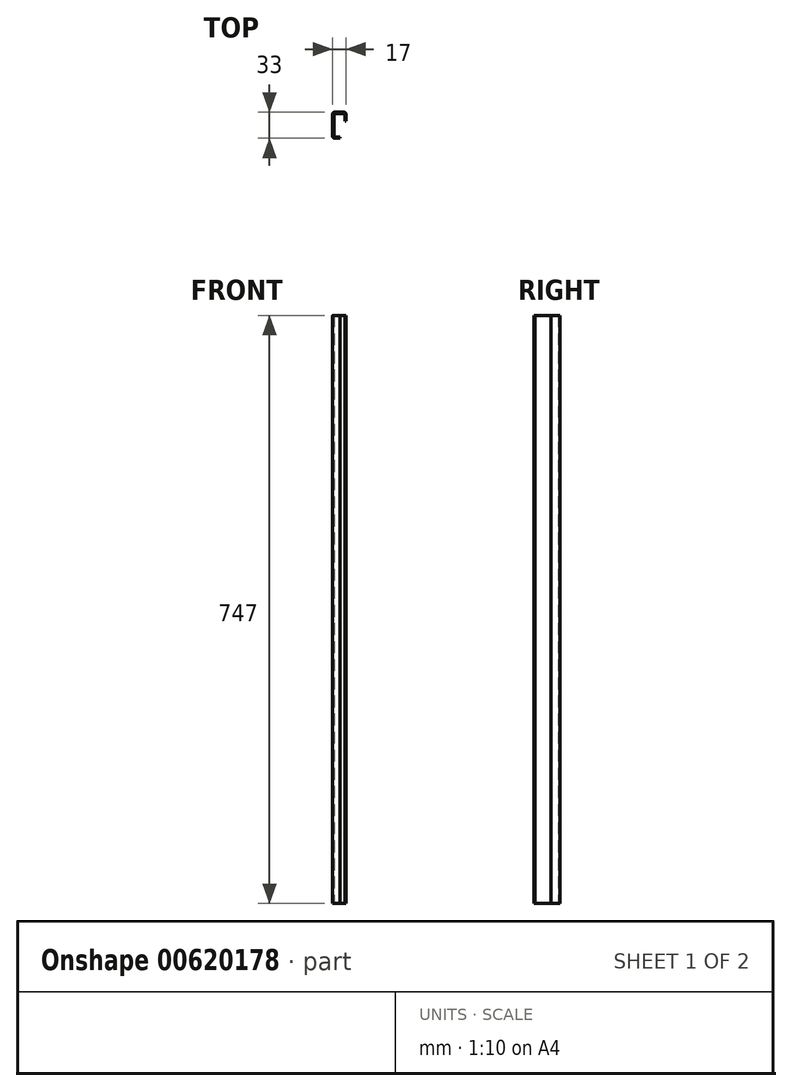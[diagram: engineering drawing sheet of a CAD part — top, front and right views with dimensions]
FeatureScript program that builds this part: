
annotation { "Feature Type Name" : "Feature", "Feature Type Description" : "" }
export const myFeature = defineFeature(function(context is Context, id is Id, definition is map)
    precondition{}
    {
        {
            var Q0;
            Q0=qCreatedBy(makeId("Top.planeOp"),FACE);
            var sketch = newSketch(context, id + "F0", { "sketchPlane" : qUnion([Q0])});
            skLineSegment(sketch, "E0", {"start": v(9.5, -16.5) * mm, "end": v(2.5, -16.5) * mm});
            skLineSegment(sketch, "E1", {"start": v(0, -14) * mm, "end": v(0, 14) * mm});
            skLineSegment(sketch, "E2", {"start": v(2.5, 16.5) * mm, "end": v(14.5, 16.5) * mm});
            skLineSegment(sketch, "E3", {"start": v(17, 14) * mm, "end": v(17, 5.5) * mm});
            skPoint(sketch, "E4.visualSharp", {"position": v(0, 16.5) * mm});
            skArc(sketch, "E4.filletArc", {"start": v(2.5, 16.5) * mm, "mid": v(0.73, 15.77) * mm, "end": v(0, 14) * mm});
            skPoint(sketch, "E5.visualSharp", {"position": v(17, 16.5) * mm});
            skArc(sketch, "E5.filletArc", {"start": v(17, 14) * mm, "mid": v(16.27, 15.77) * mm, "end": v(14.5, 16.5) * mm});
            skPoint(sketch, "E6.visualSharp", {"position": v(0, -16.5) * mm});
            skArc(sketch, "E6.filletArc", {"start": v(0, -14) * mm, "mid": v(0.73, -15.77) * mm, "end": v(2.5, -16.5) * mm});
            skLineSegment(sketch, "E7.0", {"start": v(15.5, 14) * mm, "end": v(15.5, 5.5) * mm});
            skArc(sketch, "E7.1", {"start": v(15.5, 14) * mm, "mid": v(15.2, 14.7) * mm, "end": v(14.5, 15) * mm});
            skLineSegment(sketch, "E7.2", {"start": v(2.5, 15) * mm, "end": v(14.5, 15) * mm});
            skLineSegment(sketch, "E7.3", {"start": v(9.5, -15) * mm, "end": v(2.5, -15) * mm});
            skArc(sketch, "E7.4", {"start": v(1.5, -14) * mm, "mid": v(1.8, -14.7) * mm, "end": v(2.5, -15) * mm});
            skLineSegment(sketch, "E7.5", {"start": v(1.5, -14) * mm, "end": v(1.5, 14) * mm});
            skArc(sketch, "E7.6", {"start": v(2.5, 15) * mm, "mid": v(1.8, 14.7) * mm, "end": v(1.5, 14) * mm});
            skLineSegment(sketch, "E8", {"start": v(15.5, 5.5) * mm, "end": v(17, 5.5) * mm});
            skLineSegment(sketch, "E9", {"start": v(9.5, -15) * mm, "end": v(9.5, -16.5) * mm});
            skSolve(sketch);
        }
        {
            var Q0;
            Q0=makeQuery(id+"F0.imprint","IMPRINT",FACE,{"disambiguationData":[TD([[makeQuery(id+"F0.imprint","IMPRINT",EDGE,{"derivedFrom":sQuery(id+"F0.wireOp",EDGE,"E0")}),-1.0]])]});
            extrude(context, id + "F1", {"entities" : qUnion([Q0]), "endBound" : BoundingType.SYMMETRIC, "depth" : 747 * mm, "offsetDistance" : 25 * mm});
        }
    });
